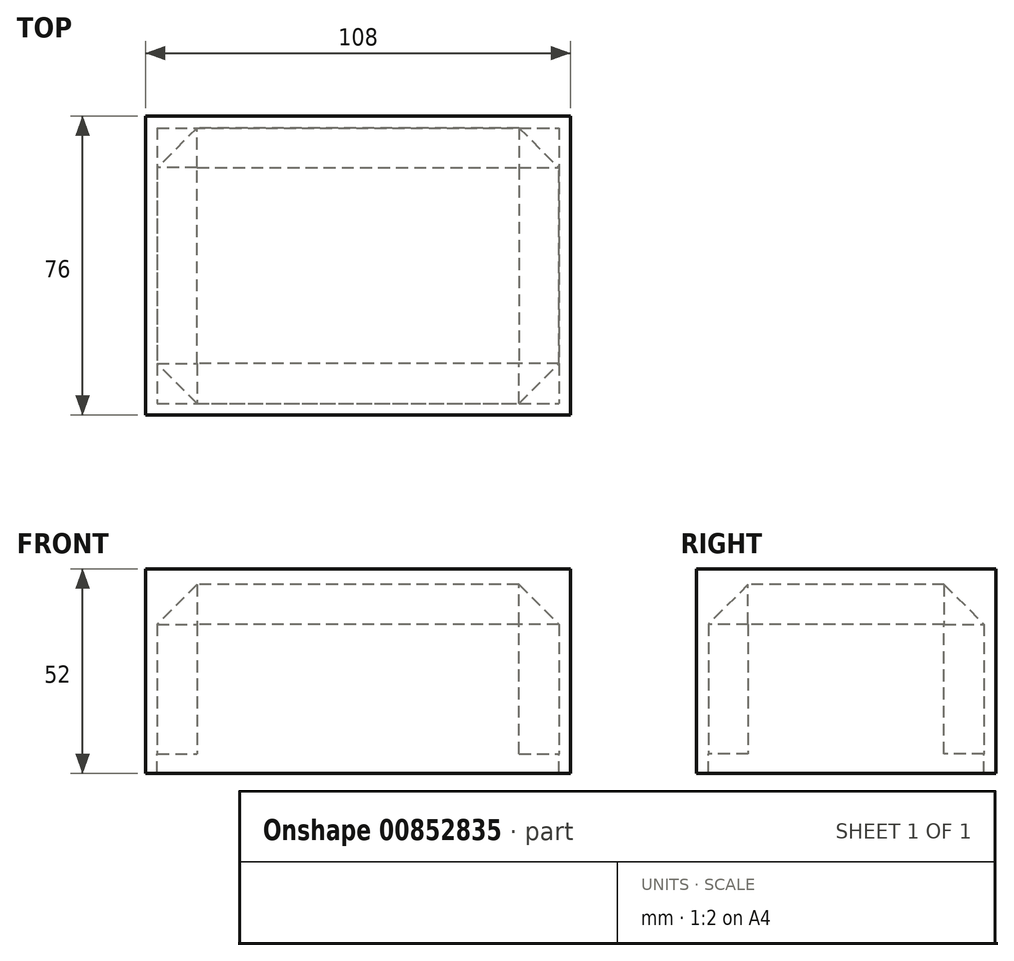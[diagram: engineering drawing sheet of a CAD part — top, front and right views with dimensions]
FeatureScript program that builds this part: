
annotation { "Feature Type Name" : "Feature", "Feature Type Description" : "" }
export const myFeature = defineFeature(function(context is Context, id is Id, definition is map)
    precondition{}
    {
        {
            var Q0;
            Q0=qCreatedBy(makeId("Top.planeOp"),FACE);
            var sketch = newSketch(context, id + "F0", { "sketchPlane" : qUnion([Q0])});
            skLineSegment(sketch, "E0.bottom", {"start": v(-51, 35) * mm, "end": v(51, 35) * mm});
            skLineSegment(sketch, "E0.top", {"start": v(-51, -35) * mm, "end": v(51, -35) * mm});
            skLineSegment(sketch, "E0.left", {"start": v(-51, 35) * mm, "end": v(-51, -35) * mm});
            skLineSegment(sketch, "E0.right", {"start": v(51, 35) * mm, "end": v(51, -35) * mm});
            skPoint(sketch, "E0.middle", {"position": v(0, 0) * mm});
            skLineSegment(sketch, "E1.0", {"start": v(-54, 38) * mm, "end": v(54, 38) * mm});
            skLineSegment(sketch, "E1.1", {"start": v(-54, 38) * mm, "end": v(-54, -38) * mm});
            skLineSegment(sketch, "E1.2", {"start": v(-54, -38) * mm, "end": v(54, -38) * mm});
            skLineSegment(sketch, "E1.3", {"start": v(54, 38) * mm, "end": v(54, -38) * mm});
            skSolve(sketch);
        }
        {
            var Q0;
            Q0=makeQuery(id+"F0.imprint","IMPRINT",FACE,{"disambiguationData":[TD([[makeQuery(id+"F0.imprint","IMPRINT",EDGE,{"derivedFrom":sQuery(id+"F0.wireOp",EDGE,"E0.bottom")}),1.0]])]});
            extrude(context, id + "F1", {"entities" : qUnion([Q0]), "depth" : 47 * mm, "offsetDistance" : 25 * mm});
        }
        {
            var Q0;
            Q0=makeQuery(id+"F0.imprint","IMPRINT",FACE,{"disambiguationData":[TD([[makeQuery(id+"F0.imprint","IMPRINT",EDGE,{"derivedFrom":sQuery(id+"F0.wireOp",EDGE,"E0.bottom")}),-1.0]])]});
            extrude(context, id + "F2", {"entities" : qUnion([Q0]), "operationType" : NewBodyOperationType.ADD, "depth" : 47 * mm, "offsetDistance" : 25 * mm, "hasSecondDirection" : true, "secondDirectionOppositeDirection" : false, "secondDirectionDepth" : 43 * mm});
        }
        {
            var Q0;
            Q0=makeQuery(id+"F2.opExtrude","CAP_FACE",FACE,{"disambiguationData":[OSD([sQuery(id+"F0.wireOp",EDGE,"E0.bottom"),sQuery(id+"F0.wireOp",EDGE,"E0.top"),sQuery(id+"F0.wireOp",EDGE,"E0.left"),sQuery(id+"F0.wireOp",EDGE,"E0.right")])],"isStart":true});
            var Q1;
            Q1=makeQuery(id+"F1.opExtrude","SWEPT_EDGE",EDGE,{"disambiguationData":[OSD([sQuery(id+"F0.wireOp",EDGE,"E0.bottom"),sQuery(id+"F0.wireOp",EDGE,"E0.right")])]});
            var Q2;
            Q2=makeQuery(id+"F1.opExtrude","SWEPT_EDGE",EDGE,{"disambiguationData":[OSD([sQuery(id+"F0.wireOp",EDGE,"E0.bottom"),sQuery(id+"F0.wireOp",EDGE,"E0.left")])]});
            var Q3;
            Q3=makeQuery(id+"F1.opExtrude","SWEPT_EDGE",EDGE,{"disambiguationData":[OSD([sQuery(id+"F0.wireOp",EDGE,"E0.top"),sQuery(id+"F0.wireOp",EDGE,"E0.left")])]});
            var Q4;
            Q4=makeQuery(id+"F1.opExtrude","SWEPT_EDGE",EDGE,{"disambiguationData":[OSD([sQuery(id+"F0.wireOp",EDGE,"E0.top"),sQuery(id+"F0.wireOp",EDGE,"E0.right")])]});
            chamfer(context, id + "F3", {"entities" : qUnion([Q0, Q1, Q2, Q3, Q4]), "width" : 10.1 * mm, "tangentPropagation" : true});
        }
        {
            var Q0;
            Q0=makeQuery(id+"F0.imprint","IMPRINT",FACE,{"disambiguationData":[TD([[makeQuery(id+"F0.imprint","IMPRINT",EDGE,{"derivedFrom":sQuery(id+"F0.wireOp",EDGE,"E0.bottom")}),1.0]])]});
            extrude(context, id + "F4", {"entities" : qUnion([Q0]), "operationType" : NewBodyOperationType.ADD, "oppositeDirection" : true, "depth" : 5 * mm, "offsetDistance" : 25 * mm});
        }
    });
